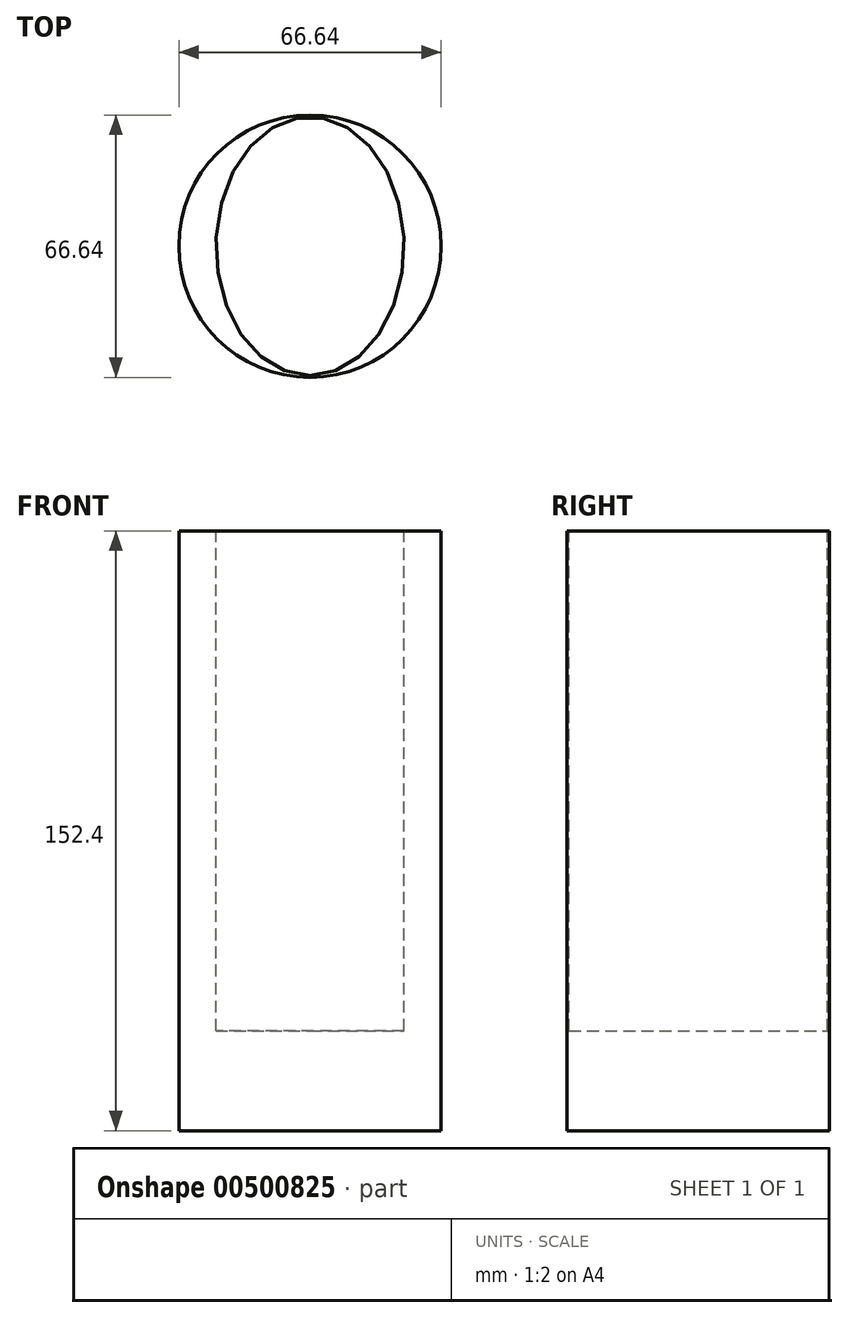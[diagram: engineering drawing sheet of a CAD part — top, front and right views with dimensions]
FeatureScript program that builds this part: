
annotation { "Feature Type Name" : "Feature", "Feature Type Description" : "" }
export const myFeature = defineFeature(function(context is Context, id is Id, definition is map)
    precondition{}
    {
        {
            var Q0;
            Q0=qCreatedBy(makeId("Top.planeOp"),FACE);
            var sketch = newSketch(context, id + "F0", { "sketchPlane" : qUnion([Q0])});
            skCircle(sketch, "E0", {"center": v(0, 0) * mm, "radius": 33.32 * mm});
            skSolve(sketch);
        }
        {
            var Q0;
            Q0 = qSketchRegion(id + "F0", true);
            extrude(context, id + "F1", {"entities" : qUnion([Q0]), "depth" : 152.4 * mm});
        }
        {
            var Q0;
            Q0=makeQuery(id+"F1.opExtrude","CAP_FACE",FACE,{"disambiguationData":[OSD([sQuery(id+"F0.wireOp",EDGE,"E0")])],"isStart":false});
            var sketch = newSketch(context, id + "F2", { "sketchPlane" : qUnion([Q0])});
            skEllipse(sketch, "E1", {"center": v(0, 0) * mm, "majorRadius": 32.8 * mm, "minorRadius": 23.9 * mm, "majorAxis": v(0, -1)});
            skSolve(sketch);
        }
        {
            var Q0;
            Q0=makeQuery(id+"F2.imprint","IMPRINT",FACE,{"disambiguationData":[TD([[makeQuery(id+"F2.imprint","IMPRINT",EDGE,{"derivedFrom":sQuery(id+"F2.wireOp",EDGE,"E1")}),1.0]])]});
            extrude(context, id + "F3", {"entities" : qUnion([Q0]), "operationType" : NewBodyOperationType.REMOVE, "oppositeDirection" : true, "depth" : 127 * mm});
        }
        {
            var Q0;
            Q0=qCreatedBy(makeId("Front.planeOp"),FACE);
            cPlane(context, id + "F4", {"entities" : qUnion([Q0]), "cplaneType" : CPlaneType.OFFSET, "offset" : 34.8 * mm, "oppositeDirection" : true, "width" : 152.4 * mm, "height" : 152.4 * mm});
        }
    });
